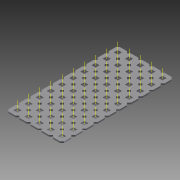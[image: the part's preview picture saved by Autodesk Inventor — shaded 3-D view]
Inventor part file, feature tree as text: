
AUTODESK INVENTOR PART (.ipt)
format: ipt  version: 2015 (Build 190159000, 159)  size: 1,132,544 bytes
history: native  units: in
note: dims shown in document units (in); Inventor stores cm internally (conversion verified against a paired STEP export)
features: other x59, extrude x2, pattern_linear x1, imported_body x1
ambient origin geometry x8: Origin, YZ Plane, XZ Plane, XY Plane, X Axis, Y Axis, Z Axis, Center Point
bodies: Body1 (feature_tree)
feature tree (63):
  other  "Diamond-Pattern"
  other  "Plate"
  extrude  "length cut"  TaperAngle=0.0deg  [1 undecoded]
  extrude  "width cut"  TaperAngle=0.0deg  [1 undecoded]
  other  "constraint axis"
  pattern_linear  "constraint axes"  Spacing1=0.5in  [1 undecoded]
  other  "front plane"
  other  "right plane"
  imported_body  "Base1"
  other  "length profile"
  other  "width profile"
  other  "Work Point1"
  other  "Work Axis36"
  other  "Work Axis37"
  other  "Work Axis38"
  other  "Work Axis39"
  other  "Work Axis40"
  other  "Work Axis41"
  other  "Work Axis42"
  other  "Work Axis43"
  other  "Work Axis44"
  other  "Work Axis45"
  other  "Work Axis46"
  other  "Work Axis47"
  other  "Work Axis48"
  other  "Work Axis49"
  other  "Work Axis50"
  other  "Work Axis51"
  other  "Work Axis52"
  other  "Work Axis53"
  other  "Work Axis54"
  other  "Work Axis55"
  other  "Work Axis56"
  other  "Work Axis57"
  other  "Work Axis58"
  other  "Work Axis59"
  other  "Work Axis60"
  other  "Work Axis61"
  other  "Work Axis62"
  other  "Work Axis63"
  other  "Work Axis64"
  other  "back plane"
  other  "left plane"
  other  "Work Axis120"
  other  "Work Axis121"
  other  "Work Axis122"
  other  "Work Axis123"
  other  "Work Axis124"
  other  "Work Axis125"
  other  "Work Axis126"
  other  "Work Axis127"
  other  "Work Axis128"
  other  "Work Axis129"
  other  "Work Axis130"
  other  "Work Axis131"
  other  "Work Axis132"
  other  "Work Axis133"
  other  "Work Axis134"
  other  "Work Axis135"
  other  "Work Axis136"
  other  "Work Axis137"
  other  "Work Axis138"
  other  "Work Axis139"
note: 3 required parameter values undecoded (feature->parameter linkage not recoverable at this tier; creation-order binding heuristic only, values carry confidence <= 0.55)
